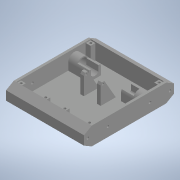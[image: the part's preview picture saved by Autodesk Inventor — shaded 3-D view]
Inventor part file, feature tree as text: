
AUTODESK INVENTOR PART (.ipt)
format: ipt  version: 2020 (Build 240168000, 168)  size: 396,288 bytes
history: native  units: in
note: dims shown in document units (in); Inventor stores cm internally (conversion verified against a paired STEP export)
features: projected_geometry x13, extrude x11, sketch x11, mirror x4, plane x1
ambient origin geometry x8: Origin, YZ Plane, XZ Plane, XY Plane, X Axis, Y Axis, Z Axis, Center Point
bodies: Solid1 (feature_tree)
feature tree (40):
  extrude  "Extrusion1"  Depth=5.9055in
  extrude  "Extrusion2"  TaperAngle=0.0deg  [1 undecoded]
  extrude  "Extrusion3"  Depth=1.063in
  extrude  "Extrusion4"  Depth=0.315in
  extrude  "Extrusion5"  TaperAngle=0.0deg  [1 undecoded]
  extrude  "Extrusion6"  Depth=0.5906in
  mirror  "Mirror1"
  extrude  "Extrusion7"  Depth=0.0787in
  mirror  "Mirror2"
  extrude  "Extrusion8"  Depth=0.5512in
  mirror  "Mirror3"
  plane  "Work Plane1"
  extrude  "Extrusion9"  Depth=0.7874in TaperAngle=0.0deg
  mirror  "Mirror4"
  extrude  "Extrusion10"  Depth=6.063in TaperAngle=0.0deg
  extrude  "Extrusion11"  Depth=0.1575in
  sketch  "Sketch1"  dims[d0=1.1811in d1=5.9055in]
  sketch  "Sketch2"  dims[d2=5.1181in d3=0.0in]
  projected_geometry  "Projected Loop1"
  sketch  "Sketch3"  dims[d4=0.1575in d5=1.063in]
  projected_geometry  "Projected Loop2"
  projected_geometry  "Projected Loop3"
  sketch  "Sketch4"  dims[d6=0.0in d8=0.315in]
  sketch  "Sketch5"  dims[d10=0.993in d11=0.0in]
  projected_geometry  "Projected Loop4"
  sketch  "Sketch6"  dims[d12=0.6496in d13=0.5906in]
  sketch  "Sketch7"  dims[d14=1.5748in d15=0.0787in]
  sketch  "Sketch9"  dims[d16=0.5512in d17=0.0in d18=0.6102in]
  sketch  "Sketch10"  dims[d19=0.4803in d20=0.7874in d21=0.0in]
  sketch  "Sketch12"  dims[d22=0.1654in d23=6.063in d24=0.0in]
  projected_geometry  "Projected Loop6"
  projected_geometry  "Projected Loop7"
  projected_geometry  "Projected Loop8"
  sketch  "Sketch13"  dims[d25=0.5114in d26=0.1575in d27=1.5748in d28=0.0in d29=0.0in d30=0.1575in d31=0.2756in d32=0.0in d33=0.4331in d34=0.122in d38=2.7559in d40=0.061in d41=0.0909in d42=0.2362in d43=0.0in d44=60.0deg d45=0.0787in d46=0.315in d48=0.993in d49=0.0in d51=0.1575in d52=0.1575in d53=0.2756in d54=0.0in d55=0.4724in]
  projected_geometry  "Projected Loop9"
  projected_geometry  "Projected Loop10"
  projected_geometry  "Projected Loop11"
  projected_geometry  "Projected Loop12"
  projected_geometry  "Projected Loop13"
  projected_geometry  "Projected Loop14"
note: 2 required parameter values undecoded (feature->parameter linkage not recoverable at this tier; creation-order binding heuristic only, values carry confidence <= 0.55)
